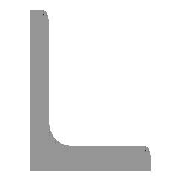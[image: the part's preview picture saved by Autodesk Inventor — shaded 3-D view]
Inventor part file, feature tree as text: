
AUTODESK INVENTOR PART (.ipt)
format: ipt  version: 2013 (Build 170138000, 138)  size: 130,048 bytes
history: native  units: mm (DEFAULTED — no unit token found)
features: other x4, plane x3, split x2, sketch x2
ambient origin geometry x8: Origin, YZ Plane, XZ Plane, XY Plane, X Axis, Y Axis, Z Axis, Center Point
bodies: Solid1 (feature_tree), Body (feature_tree)
feature tree (11):
  parser-record x1  (decoder bookkeeping rows leaked as tree rows — omitted from the tree; the rows remain in map.json)
  other  "Driven Length"
  other  "Start plane"
  other  "End plane"
  plane  "Work Plane4"
  split  "Split1"
  plane  "Work Plane5"
  split  "Split2"
  sketch  "Sketch3"  dims[d0=38.1mm]
  plane  "Work Plane3"
  sketch  "Sketch4"  dims[d1=38.1mm d2=4.7625mm d3=4.7625mm d4=561.975mm d5=0.0mm d10=0.0mm d11=0.0mm d12=-0.0mm d13=561.975mm d14=4.826mm d15=2.286mm d16=90.0deg d17=561.975mm]
